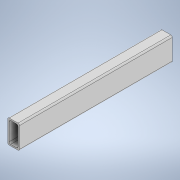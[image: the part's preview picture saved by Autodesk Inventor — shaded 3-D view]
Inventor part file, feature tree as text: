
AUTODESK INVENTOR PART (.ipt)
format: ipt  version: 2020 (Build 240168000, 168)  size: 125,952 bytes
history: native  units: in
note: dims shown in document units (in); Inventor stores cm internally (conversion verified against a paired STEP export)
features: extrude x1, sketch x1
ambient origin geometry x8: Origin, YZ Plane, XZ Plane, XY Plane, X Axis, Y Axis, Z Axis, Center Point
bodies: Solid1 (feature_tree)
feature tree (2):
  extrude  "Extrusion1"  Depth=1.0in
  sketch  "Sketch1"  dims[d0=2.0in d1=1.0in d2=0.125in d3=0.125in d4=0.125in d5=0.125in d6=0.125in d7=0.125in d8=0.125in d9=0.125in d10=0.125in d11=13.0in d12=0.0in]
